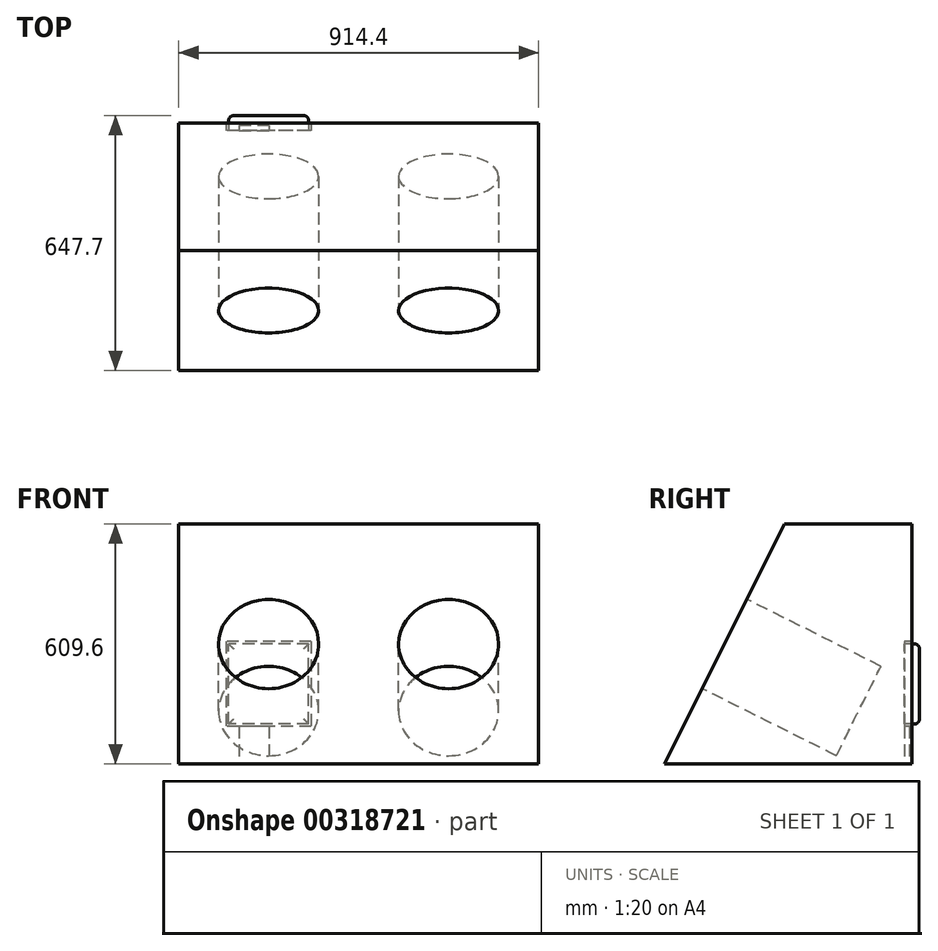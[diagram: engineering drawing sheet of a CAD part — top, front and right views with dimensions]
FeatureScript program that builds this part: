
annotation { "Feature Type Name" : "Feature", "Feature Type Description" : "" }
export const myFeature = defineFeature(function(context is Context, id is Id, definition is map)
    precondition{}
    {
        {
            var Q0;
            Q0=qCreatedBy(makeId("Top.planeOp"),FACE);
            var sketch = newSketch(context, id + "F0", { "sketchPlane" : qUnion([Q0])});
            skLineSegment(sketch, "E0.bottom", {"start": v(0, 0) * mm, "end": v(0, 0) * mm});
            skLineSegment(sketch, "E0.top", {"start": v(0, 0) * mm, "end": v(0, 0) * mm});
            skLineSegment(sketch, "E0.left", {"start": v(0, 0) * mm, "end": v(0, 0) * mm});
            skLineSegment(sketch, "E0.right", {"start": v(0, 0) * mm, "end": v(0, 0) * mm});
            skLineSegment(sketch, "E1.bottom", {"start": v(0, 0) * mm, "end": v(914.4, 0) * mm});
            skLineSegment(sketch, "E1.top", {"start": v(0, 609.6) * mm, "end": v(914.4, 609.6) * mm});
            skLineSegment(sketch, "E1.left", {"start": v(0, 0) * mm, "end": v(0, 609.6) * mm});
            skLineSegment(sketch, "E1.right", {"start": v(914.4, 0) * mm, "end": v(914.4, 609.6) * mm});
            skSolve(sketch);
        }
        {
            var Q0;
            Q0 = qSketchRegion(id + "F0", true);
            extrude(context, id + "F1", {"entities" : qUnion([Q0]), "depth" : 609.6 * mm});
        }
        {
            var Q0;
            Q0=makeQuery(id+"F1.opExtrude","SWEPT_FACE",FACE,{"disambiguationData":[OSD([sQuery(id+"F0.wireOp",EDGE,"E1.left")])]});
            var sketch = newSketch(context, id + "F2", { "sketchPlane" : qUnion([Q0])});
            skLineSegment(sketch, "E2", {"start": v(-609.6, 609.6) * mm, "end": v(-304.8, 609.6) * mm});
            skLineSegment(sketch, "E3", {"start": v(-304.8, 609.6) * mm, "end": v(0, 0) * mm});
            skSolve(sketch);
        }
        {
            var Q0;
            {var subQ0=sQuery(id+"F2.wireOp",EDGE,"E3");Q0=makeQuery(id+"F2.imprint","IMPRINT",FACE,{"disambiguationData":[TD([[makeQuery(id+"F2.imprint","IMPRINT",EDGE,{"derivedFrom":subQ0}),1.0]])]});}
            extrude(context, id + "F3", {"entities" : qUnion([Q0]), "operationType" : NewBodyOperationType.REMOVE, "endBound" : BoundingType.THROUGH_ALL, "oppositeDirection" : true, "depth" : 25.4 * mm});
        }
        {
            var Q0;
            Q0=makeQuery(id+"F3.boolean.opBoolean","COPY",FACE,{"derivedFrom":makeQuery(id+"F3.opExtrude","SWEPT_FACE",FACE,{"disambiguationData":[OSD([sQuery(id+"F2.wireOp",EDGE,"E3")])]})});
            var sketch = newSketch(context, id + "F4", { "sketchPlane" : qUnion([Q0])});
            skCircle(sketch, "E4", {"center": v(228.6, 340.78) * mm, "radius": 127 * mm});
            skCircle(sketch, "E5", {"center": v(685.8, 340.78) * mm, "radius": 127 * mm});
            skLineSegment(sketch, "E6", {"start": v(457.2, 681.55) * mm, "end": v(457.2, -30.88) * mm, "construction": true});
            skPoint(sketch, "E7.start.orphan", {"position": v(0, 340.78) * mm});
            skPoint(sketch, "E8.trimOffspring.end.orphan", {"position": v(914.4, 340.78) * mm});
            skLineSegment(sketch, "E9", {"start": v(0, 340.78) * mm, "end": v(914.4, 340.78) * mm, "construction": true});
            skSolve(sketch);
        }
        {
            var Q0;
            Q0=makeQuery(id+"F4.imprint","IMPRINT",FACE,{"disambiguationData":[TD([[makeQuery(id+"F4.imprint","IMPRINT",EDGE,{"derivedFrom":sQuery(id+"F4.wireOp",EDGE,"E4")}),1.0]])]});
            var Q1;
            Q1=makeQuery(id+"F4.imprint","IMPRINT",FACE,{"disambiguationData":[TD([[makeQuery(id+"F4.imprint","IMPRINT",EDGE,{"derivedFrom":sQuery(id+"F4.wireOp",EDGE,"E5")}),1.0]])]});
            var Q2;
            Q2=makeQuery(id+"F1.opExtrude","SWEPT_FACE",FACE,{"disambiguationData":[OSD([sQuery(id+"F0.wireOp",EDGE,"E1.top")])]});
            var Q3;
            Q3=makeQuery(id+"F1.opExtrude","SWEPT_BODY",BODY,{"disambiguationData":[OSD([sQuery(id+"F0.wireOp",EDGE,"E1.bottom"),sQuery(id+"F0.wireOp",EDGE,"E1.top"),sQuery(id+"F0.wireOp",EDGE,"E1.left"),sQuery(id+"F0.wireOp",EDGE,"E1.right")])]});
            extrude(context, id + "F5", {"entities" : qUnion([Q0, Q1]), "operationType" : NewBodyOperationType.REMOVE, "oppositeDirection" : true, "endBoundEntityFace" : qUnion([Q2]), "endBoundEntityBody" : qUnion([Q3]), "depth" : 381 * mm});
        }
        {
            var Q0;
            Q0=makeQuery(id+"F1.opExtrude","SWEPT_FACE",FACE,{"disambiguationData":[OSD([sQuery(id+"F0.wireOp",EDGE,"E1.top")])]});
            var sketch = newSketch(context, id + "F6", { "sketchPlane" : qUnion([Q0])});
            skLineSegment(sketch, "E10.bottom", {"start": v(-330.2, 101.6) * mm, "end": v(-127, 101.6) * mm});
            skLineSegment(sketch, "E10.top", {"start": v(-330.2, 304.8) * mm, "end": v(-127, 304.8) * mm});
            skLineSegment(sketch, "E10.left", {"start": v(-330.2, 101.6) * mm, "end": v(-330.2, 304.8) * mm});
            skLineSegment(sketch, "E10.right", {"start": v(-127, 101.6) * mm, "end": v(-127, 304.8) * mm});
            skSolve(sketch);
        }
        {
            var Q0;
            Q0=makeQuery(id+"F6.imprint","IMPRINT",FACE,{"disambiguationData":[TD([[makeQuery(id+"F6.imprint","IMPRINT",EDGE,{"derivedFrom":sQuery(id+"F6.wireOp",EDGE,"E10.bottom")}),1.0]])]});
            extrude(context, id + "F7", {"entities" : qUnion([Q0]), "operationType" : NewBodyOperationType.ADD, "depth" : 38.1 * mm});
        }
        {
            var Q0;
            Q0=makeQuery(id+"F7.opExtrude","CAP_EDGE",EDGE,{"disambiguationData":[OSD([sQuery(id+"F6.wireOp",EDGE,"E10.right")])],"isStart":false});
            var Q1;
            Q1=makeQuery(id+"F7.opExtrude","CAP_EDGE",EDGE,{"disambiguationData":[OSD([sQuery(id+"F6.wireOp",EDGE,"E10.top")])],"isStart":false});
            var Q2;
            Q2=makeQuery(id+"F7.opExtrude","CAP_EDGE",EDGE,{"disambiguationData":[OSD([sQuery(id+"F6.wireOp",EDGE,"E10.left")])],"isStart":false});
            var Q3;
            Q3=makeQuery(id+"F7.opExtrude","CAP_EDGE",EDGE,{"disambiguationData":[OSD([sQuery(id+"F6.wireOp",EDGE,"E10.bottom")])],"isStart":false});
            fillet(context, id + "F8", {"entities" : qUnion([Q0, Q1, Q2, Q3]), "radius" : 12.7 * mm, "tangentPropagation" : true, "allowEdgeOverflow" : false});
        }
        {
            var Q0;
            Q0=makeQuery(id+"F1.opExtrude","SWEPT_FACE",FACE,{"disambiguationData":[OSD([sQuery(id+"F0.wireOp",EDGE,"E1.top")])]});
            var sketch = newSketch(context, id + "F9", { "sketchPlane" : qUnion([Q0])});
            skLineSegment(sketch, "E11.bottom", {"start": v(-914.4, 609.6) * mm, "end": v(0, 609.6) * mm});
            skLineSegment(sketch, "E11.top", {"start": v(-914.4, 0) * mm, "end": v(0, 0) * mm});
            skLineSegment(sketch, "E11.left", {"start": v(-914.4, 609.6) * mm, "end": v(-914.4, 0) * mm});
            skLineSegment(sketch, "E11.right", {"start": v(0, 609.6) * mm, "end": v(0, 0) * mm});
            skLineSegment(sketch, "E12.bottom", {"start": v(-336.55, 311.15) * mm, "end": v(-120.65, 311.15) * mm});
            skLineSegment(sketch, "E12.top", {"start": v(-336.55, 95.25) * mm, "end": v(-229.87, 95.25) * mm});
            skLineSegment(sketch, "E12.left", {"start": v(-336.55, 311.15) * mm, "end": v(-336.55, 95.25) * mm});
            skLineSegment(sketch, "E12.right", {"start": v(-120.65, 311.15) * mm, "end": v(-120.65, 95.25) * mm});
            skLineSegment(sketch, "E13.top", {"start": v(-229.87, 0) * mm, "end": v(-153.67, 0) * mm});
            skLineSegment(sketch, "E13.left", {"start": v(-229.87, 95.25) * mm, "end": v(-229.87, 0) * mm});
            skLineSegment(sketch, "E13.right", {"start": v(-153.67, 95.25) * mm, "end": v(-153.67, 0) * mm});
            skLineSegment(sketch, "E14.trimOffspring", {"start": v(-153.67, 95.25) * mm, "end": v(-120.65, 95.25) * mm});
            skSolve(sketch);
        }
        {
            var Q0;
            Q0=makeQuery(id+"F9.imprint","IMPRINT",FACE,{"disambiguationData":[TD([[makeQuery(id+"F9.imprint","IMPRINT",EDGE,{"derivedFrom":sQuery(id+"F9.wireOp",EDGE,"E11.bottom")}),1.0]])]});
            extrude(context, id + "F10", {"entities" : qUnion([Q0]), "operationType" : NewBodyOperationType.ADD, "depth" : 19.05 * mm});
        }
        {
            var Q0;
            Q0=makeQuery(id+"F10.opExtrude","CAP_FACE",FACE,{"disambiguationData":[OSD([sQuery(id+"F9.wireOp",EDGE,"E11.bottom"),sQuery(id+"F9.wireOp",EDGE,"E11.top"),sQuery(id+"F9.wireOp",EDGE,"E11.left"),sQuery(id+"F9.wireOp",EDGE,"E11.right"),sQuery(id+"F9.wireOp",EDGE,"E12.bottom"),sQuery(id+"F9.wireOp",EDGE,"E12.top"),sQuery(id+"F9.wireOp",EDGE,"E12.left"),sQuery(id+"F9.wireOp",EDGE,"E12.right"),sQuery(id+"F9.wireOp",EDGE,"E13.left"),sQuery(id+"F9.wireOp",EDGE,"E13.right"),sQuery(id+"F9.wireOp",EDGE,"E14.trimOffspring")])],"isStart":false});
            var sketch = newSketch(context, id + "F11", { "sketchPlane" : qUnion([Q0])});
            skLineSegment(sketch, "E15.bottom", {"start": v(-229.87, 95.25) * mm, "end": v(-153.67, 95.25) * mm});
            skLineSegment(sketch, "E15.top", {"start": v(-229.87, 0) * mm, "end": v(-153.67, 0) * mm});
            skLineSegment(sketch, "E15.left", {"start": v(-229.87, 95.25) * mm, "end": v(-229.87, 0) * mm});
            skLineSegment(sketch, "E15.right", {"start": v(-153.67, 95.25) * mm, "end": v(-153.67, 0) * mm});
            skSolve(sketch);
        }
        {
            var Q0;
            Q0=makeQuery(id+"F11.imprint","IMPRINT",FACE,{"disambiguationData":[TD([[makeQuery(id+"F11.imprint","IMPRINT",EDGE,{"derivedFrom":sQuery(id+"F11.wireOp",EDGE,"E15.bottom")}),-1.0]])]});
            extrude(context, id + "F12", {"entities" : qUnion([Q0]), "operationType" : NewBodyOperationType.ADD, "oppositeDirection" : true, "depth" : 6.35 * mm});
        }
    });
